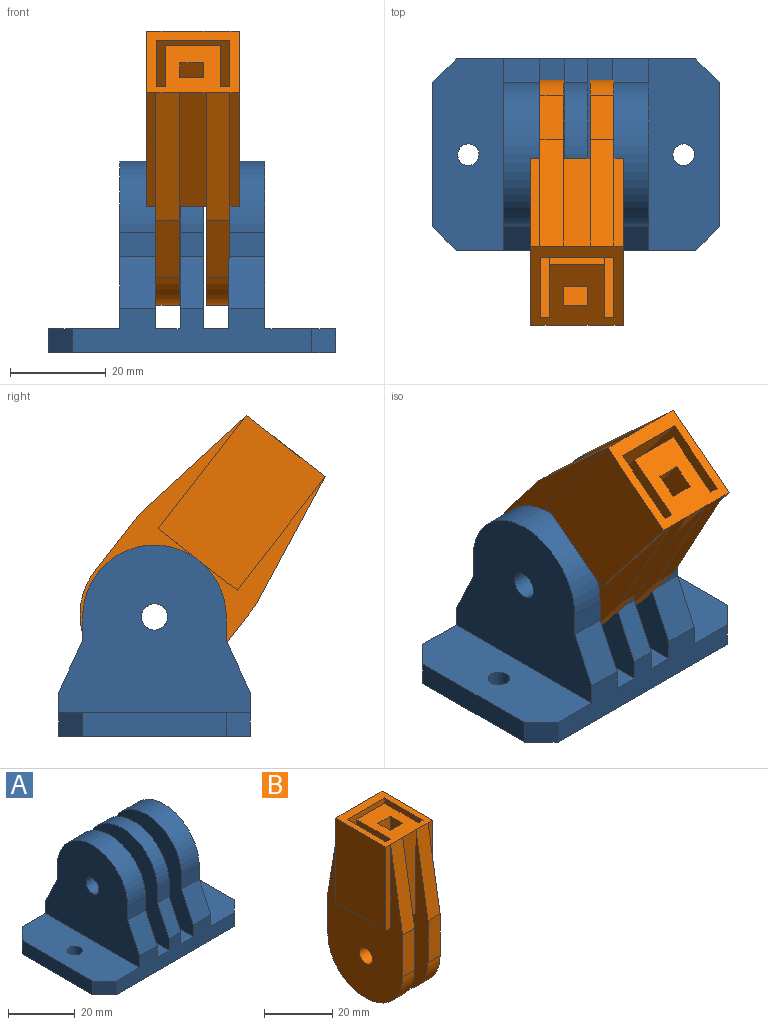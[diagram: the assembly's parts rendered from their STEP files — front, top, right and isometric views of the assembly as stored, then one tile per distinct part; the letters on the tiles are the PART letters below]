
ASSEMBLY  parts=2 mates=1
PART A: 46 faces, bbox 60x40x40 mm
  f0: plane 40x14.78mm, normal (0,0,1), area 550.1mm2, adj f3,f6,f8,f9,f35,f38,f39
  f1: plane 40x5.07mm, normal (0,0,1), area 202.7mm2, adj f6,f8,f14,f20
  f2: plane 40x5.22mm, normal (0,0,1), area 208.9mm2, adj f6,f8,f12,f15
  f3: plane 40x35mm, normal (1,0,0), area 982.8mm2, adj f0,f6,f8,f16,f17,f25,f27,f28
  f4: cylinder r=2.75mm len=5.5mm, axis (-1,0,0), area 60.5mm2, adj f15,f33
  f5: plane 40x14.93mm, normal (0,0,1), area 556.4mm2, adj f6,f7,f8,f18,f34,f36,f37
  f6: plane 50x9.29mm, normal (0,1,0), area 335.7mm2, adj f0,f1,f2,f3,f5,f10,f12,f14
  f7: plane 30x5mm, normal (-1,0,0), area 150mm2, adj f5,f10,f36,f37
  f8: plane 50x9.29mm, normal (0,-1,0), area 335.7mm2, adj f0,f1,f2,f3,f5,f10,f12,f14
  f9: plane 30x5mm, normal (1,0,0), area 150mm2, adj f0,f10,f38,f39
  f10: plane 60x40mm, normal (0,0,-1), area 2318.2mm2, adj f6,f7,f8,f9,f34,f35,f36,f37
  f11: plane 5x5mm, normal (0,-1,0), area 25mm2, adj f12,f14,f26,f41
  f12: plane 40x35mm, normal (1,0,0), area 1026.1mm2, adj f2,f6,f8,f11,f13,f23,f26,f41
  f13: plane 5x5mm, normal (0,1,0), area 25mm2, adj f12,f14,f26,f44
  f14: plane 40x35mm, normal (-1,0,0), area 1026.1mm2, adj f1,f6,f8,f11,f13,f23,f26,f41
  f15: plane 40x35mm, normal (-1,0,0), area 1026.1mm2, adj f2,f4,f6,f8,f16,f17,f25,f40
  f16: plane 7.5x5mm, normal (0,-1,0), area 37.5mm2, adj f3,f15,f25,f40
  f17: plane 7.5x5mm, normal (0,1,0), area 37.5mm2, adj f3,f15,f25,f45
  f18: plane 40x35mm, normal (-1,0,0), area 1026.1mm2, adj f5,f6,f8,f19,f21,f22,f24,f42
  f19: plane 7.5x5mm, normal (0,-1,0), area 37.5mm2, adj f18,f20,f24,f42
  f20: plane 40x35mm, normal (1,0,0), area 1026.1mm2, adj f1,f6,f8,f19,f21,f22,f24,f42
  f21: plane 7.5x5mm, normal (0,1,0), area 37.5mm2, adj f18,f20,f24,f43
  f22: cylinder r=2.75mm len=7.5mm, axis (-1,0,0), area 129.6mm2, adj f18,f20
  f23: cylinder r=2.75mm len=5.5mm, axis (-1,0,0), area 86.4mm2, adj f12,f14
  f24: cylinder r=15mm len=30mm, axis (1,0,0), area 353.4mm2, adj f18,f19,f20,f21
  f25: cylinder r=15mm len=30mm, axis (1,0,0), area 353.4mm2, adj f3,f15,f16,f17
  f26: cylinder r=15mm len=30mm, axis (-1,0,0), area 235.6mm2, adj f11,f12,f13,f14
  f27: plane 4.4x4mm, normal (0,0.5,-0.87), area 20.3mm2, adj f3,f28,f32,f33
  f28: plane 5.08x4mm, normal (0,1,0), area 20.3mm2, adj f3,f27,f29,f33
  f29: plane 4.4x4mm, normal (0,0.5,0.87), area 20.3mm2, adj f3,f28,f30,f33
  f30: plane 4.4x4mm, normal (0,-0.5,0.87), area 20.3mm2, adj f3,f29,f31,f33
  f31: plane 5.08x4mm, normal (0,-1,0), area 20.3mm2, adj f3,f30,f32,f33
  f32: plane 4.4x4mm, normal (0,-0.5,-0.87), area 20.3mm2, adj f3,f27,f31,f33
  f33: plane 10.16x8.8mm, normal (1,0,0), area 43.3mm2, adj f4,f27,f28,f29,f30,f31,f32
  f34: cylinder r=2.25mm len=5mm, axis (0,0,1), area 70.7mm2, adj f5,f10
  f35: cylinder r=2.25mm len=5mm, axis (0,0,1), area 70.7mm2, adj f0,f10
  f36: plane 5x5mm, normal (-0.71,-0.71,0), area 35.4mm2, adj f5,f7,f8,f10
  f37: plane 5x5mm, normal (-0.71,0.71,0), area 35.4mm2, adj f5,f6,f7,f10
  f38: plane 5x5mm, normal (0.71,0.71,0), area 35.4mm2, adj f0,f6,f9,f10
  f39: plane 5x5mm, normal (0.71,-0.71,0), area 35.4mm2, adj f0,f8,f9,f10
  f40: plane 10.71x7.5mm, normal (0,-0.91,0.42), area 88.7mm2, adj f3,f8,f15,f16
  f41: plane 10.71x5mm, normal (0,-0.91,0.42), area 59.1mm2, adj f8,f11,f12,f14
  f42: plane 10.71x7.5mm, normal (0,-0.91,0.42), area 88.7mm2, adj f8,f18,f19,f20
  f43: plane 10.71x7.5mm, normal (0,0.91,0.42), area 88.7mm2, adj f6,f18,f20,f21
  f44: plane 10.71x5mm, normal (0,0.91,0.42), area 59.1mm2, adj f6,f12,f13,f14
  f45: plane 10.71x7.5mm, normal (0,0.91,0.42), area 88.7mm2, adj f3,f6,f15,f17
PART B: 50 faces, bbox 19.4x30.9x60 mm
  f0: plane 16x5.5mm, normal (0,0,-1), area 59mm2, adj f2,f17,f25,f29,f48,f49
  f1: plane 30x5.5mm, normal (0,1,0), area 165mm2, adj f6,f19,f25,f29
  f2: plane 30x5.5mm, normal (0,-1,0), area 165mm2, adj f0,f19,f25,f29
  f3: plane 30x1.95mm, normal (0,1,0), area 58.5mm2, adj f5,f9,f19,f27
  f4: plane 30x1.95mm, normal (0,-1,0), area 58.5mm2, adj f5,f9,f19,f27
  f5: plane 20.9x1.95mm, normal (0,0,-1), area 40.8mm2, adj f3,f4,f9,f27
  f6: plane 5.5x3mm, normal (0,0,-1), area 16.5mm2, adj f1,f13,f25,f29
  f7: plane 30x20.9mm, normal (-1,0,0), area 627mm2, adj f8,f18,f19,f20
  f8: plane 30x1.95mm, normal (0,-1,0), area 58.5mm2, adj f7,f19,f20,f23
  f9: plane 30x20.9mm, normal (1,0,0), area 627mm2, adj f3,f4,f5,f19
  f10: plane 30x14mm, normal (-1,0,0), area 420mm2, adj f11,f17,f19,f21
  f11: plane 30x1.9mm, normal (0,1,0), area 57mm2, adj f10,f12,f19,f21
  f12: plane 30x15.9mm, normal (1,0,0), area 477mm2, adj f11,f13,f19,f21
  f13: plane 30x15.4mm, normal (0,-1,0), area 462mm2, adj f6,f12,f14,f19,f21,f32
  f14: plane 30x15.9mm, normal (-1,0,0), area 477mm2, adj f13,f15,f19,f32
  f15: plane 30x1.9mm, normal (0,1,0), area 57mm2, adj f14,f16,f19,f32
  f16: plane 30x14mm, normal (1,0,0), area 420mm2, adj f15,f17,f19,f32
  f17: plane 30x11.6mm, normal (0,1,0), area 348mm2, adj f0,f10,f16,f19,f21,f32,f43
  f18: plane 30x1.95mm, normal (0,1,0), area 58.5mm2, adj f7,f19,f20,f23
  f19: plane 20.9x19.4mm, normal (0,0,1), area 298mm2, adj f1,f2,f3,f4,f7,f8,f9,f10
  f20: plane 20.9x1.95mm, normal (0,0,-1), area 40.8mm2, adj f7,f8,f18,f23
  f21: plane 15.9x4.95mm, normal (0,0,1), area 36mm2, adj f10,f11,f12,f13,f17,f25
  f22: plane 15x5mm, normal (0,1,0), area 75mm2, adj f23,f25,f38,f40
  f23: plane 60x30.9mm, normal (-1,0,0), area 956.7mm2, adj f8,f18,f20,f22,f24,f26,f34,f37
  f24: plane 15x5mm, normal (0,-1,0), area 75mm2, adj f23,f25,f37,f39
  f25: plane 60x30.9mm, normal (1,0,0), area 1111mm2, adj f0,f1,f2,f6,f19,f21,f22,f24
  f26: plane 5x0.9mm, normal (0,0,-1), area 4.5mm2, adj f23,f25,f39,f40
  f27: plane 60x30.9mm, normal (1,0,0), area 956.7mm2, adj f3,f4,f5,f28,f30,f31,f33,f35
  f28: plane 15x5mm, normal (0,1,0), area 75mm2, adj f27,f29,f36,f41
  f29: plane 60x30.9mm, normal (-1,0,0), area 956.7mm2, adj f0,f1,f2,f6,f28,f30,f31,f32
  f30: plane 15x5mm, normal (0,-1,0), area 75mm2, adj f27,f29,f35,f42
  f31: plane 5x0.9mm, normal (0,0,-1), area 4.5mm2, adj f27,f29,f41,f42
  f32: plane 15.9x4.95mm, normal (0,0,1), area 36mm2, adj f13,f14,f15,f16,f17,f29
  f33: cylinder r=2.75mm len=5.5mm, axis (1,0,0), area 86.4mm2, adj f27,f29
  f34: cylinder r=2.75mm len=5.5mm, axis (1,0,0), area 86.4mm2, adj f23,f25
  f35: plane 30x5mm, normal (0,-0.99,0.16), area 152.1mm2, adj f19,f27,f29,f30
  f36: plane 30x5mm, normal (0,0.99,0.16), area 152.1mm2, adj f19,f27,f28,f29
  f37: plane 30x5mm, normal (0,-0.99,0.16), area 152.1mm2, adj f19,f23,f24,f25
  f38: plane 30x5mm, normal (0,0.99,0.16), area 152.1mm2, adj f19,f22,f23,f25
  f39: cylinder r=15mm len=15mm, axis (-1,0,0), area 117.8mm2, adj f23,f24,f25,f26
  f40: cylinder r=15mm len=15mm, axis (1,0,0), area 117.8mm2, adj f22,f23,f25,f26
  f41: cylinder r=15mm len=15mm, axis (1,0,0), area 117.8mm2, adj f27,f28,f29,f31
  f42: cylinder r=15mm len=15mm, axis (-1,0,0), area 117.8mm2, adj f27,f29,f30,f31
  f43: plane 5x2.87mm, normal (0,-0.71,-0.71), area 20.3mm2, adj f17,f25,f44,f49
  f44: cylinder r=10mm len=7.07mm, axis (-1,0,0), area 39.3mm2, adj f25,f43,f45,f49
  f45: plane 20.06x5mm, normal (0,-1,0), area 100.3mm2, adj f19,f25,f44,f49
  f46: plane 20.86x5mm, normal (0,1,0), area 104.3mm2, adj f19,f25,f47,f49
  f47: cylinder r=10mm len=7.07mm, axis (-1,0,0), area 39.3mm2, adj f25,f46,f48,f49
  f48: plane 5x2.07mm, normal (0,0.71,0.71), area 14.6mm2, adj f0,f25,f47,f49
  f49: plane 30x10.8mm, normal (-1,0,0), area 154.3mm2, adj f0,f19,f43,f44,f45,f46,f47,f48
PLACE A t=(-3.59,-0.1,-18.02)mm fixed
PLACE B rot(axis=(1,0,0),37.9deg) t=(-3.41,-9.31,18.82)mm
MATE revolute B.f33 <-> A.f4  axis (-1,0,0) through (-11.16,-0.1,6.98)mm
